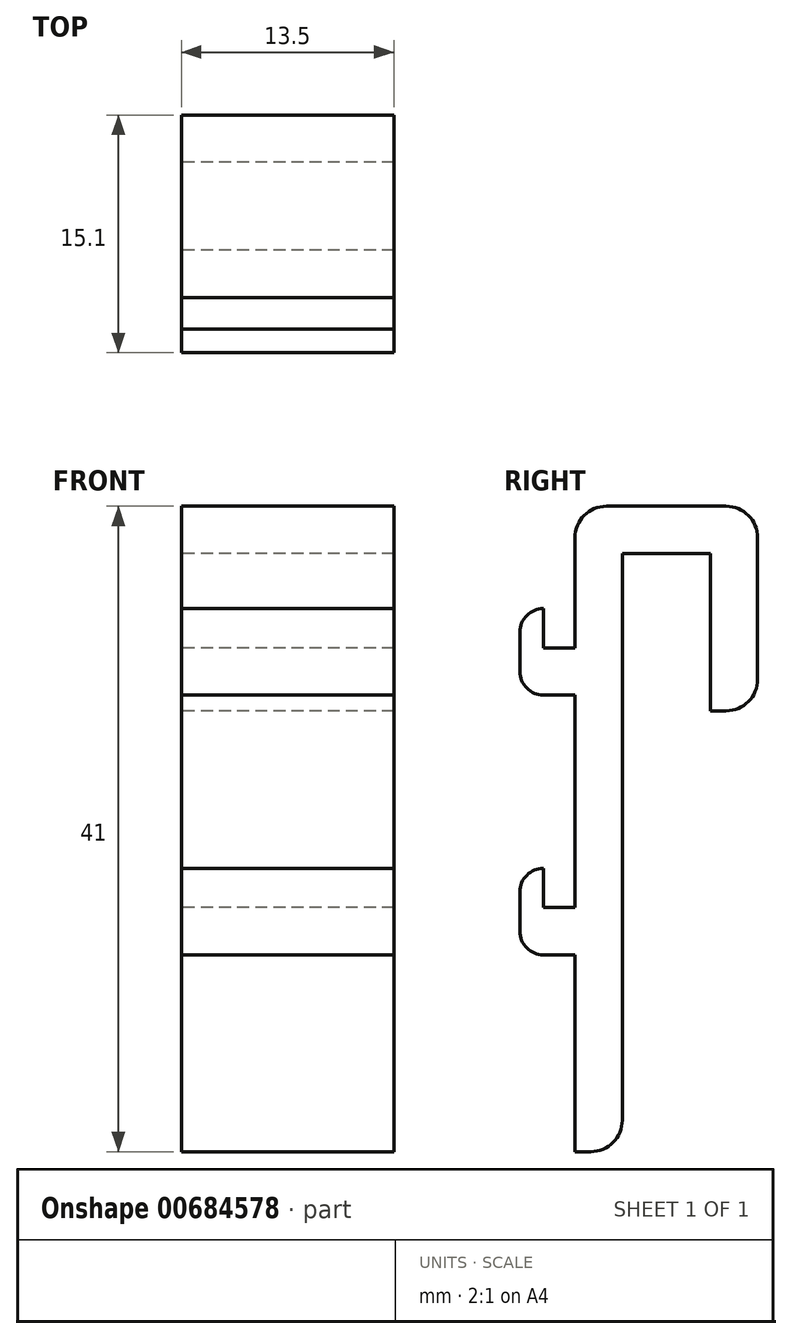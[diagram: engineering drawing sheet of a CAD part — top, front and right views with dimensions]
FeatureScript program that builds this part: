
annotation { "Feature Type Name" : "Feature", "Feature Type Description" : "" }
export const myFeature = defineFeature(function(context is Context, id is Id, definition is map)
    precondition{}
    {
        {
            var Q0;
            Q0=qCreatedBy(makeId("Top.planeOp"),FACE);
            var sketch = newSketch(context, id + "F0", { "sketchPlane" : qUnion([Q0])});
            skLineSegment(sketch, "E0", {"start": v(0, 0) * mm, "end": v(0, 12.5) * mm});
            skLineSegment(sketch, "E1", {"start": v(0, 12.5) * mm, "end": v(-3.5, 12.5) * mm});
            skLineSegment(sketch, "E2", {"start": v(-3.5, 12.5) * mm, "end": v(-3.5, 18) * mm});
            skLineSegment(sketch, "E3", {"start": v(-3.5, 18) * mm, "end": v(-2, 18) * mm});
            skLineSegment(sketch, "E4", {"start": v(-2, 18) * mm, "end": v(-2, 15.5) * mm});
            skLineSegment(sketch, "E5", {"start": v(-2, 15.5) * mm, "end": v(0, 15.5) * mm});
            skLineSegment(sketch, "E6", {"start": v(0, 15.5) * mm, "end": v(0, 29) * mm});
            skLineSegment(sketch, "E7", {"start": v(0, 29) * mm, "end": v(-3.5, 29) * mm});
            skLineSegment(sketch, "E8", {"start": v(-3.5, 29) * mm, "end": v(-3.5, 34.5) * mm});
            skLineSegment(sketch, "E9", {"start": v(-3.5, 34.5) * mm, "end": v(-2, 34.5) * mm});
            skLineSegment(sketch, "E10", {"start": v(-2, 34.5) * mm, "end": v(-2, 32) * mm});
            skLineSegment(sketch, "E11", {"start": v(-2, 32) * mm, "end": v(0, 32) * mm});
            skLineSegment(sketch, "E12", {"start": v(0, 32) * mm, "end": v(0, 41) * mm});
            skLineSegment(sketch, "E13", {"start": v(0, 41) * mm, "end": v(11.6, 41) * mm});
            skLineSegment(sketch, "E14", {"start": v(11.6, 41) * mm, "end": v(11.6, 28) * mm});
            skLineSegment(sketch, "E15", {"start": v(11.6, 28) * mm, "end": v(8.6, 28) * mm});
            skLineSegment(sketch, "E16", {"start": v(8.6, 28) * mm, "end": v(8.6, 38) * mm});
            skLineSegment(sketch, "E17", {"start": v(8.6, 38) * mm, "end": v(3, 38) * mm});
            skLineSegment(sketch, "E18", {"start": v(3, 38) * mm, "end": v(3, 0) * mm});
            skLineSegment(sketch, "E19", {"start": v(3, 0) * mm, "end": v(0, 0) * mm});
            skSolve(sketch);
        }
        {
            var Q0;
            Q0=makeQuery(id+"F0.imprint","IMPRINT",FACE,{"disambiguationData":[TD([[makeQuery(id+"F0.imprint","IMPRINT",EDGE,{"derivedFrom":sQuery(id+"F0.wireOp",EDGE,"E0")}),-1.0]])]});
            extrude(context, id + "F1", {"entities" : qUnion([Q0]), "depth" : 13.5 * mm});
        }
        {
            var Q0;
            Q0=makeQuery(id+"F1.opExtrude","SWEPT_EDGE",EDGE,{"disambiguationData":[OSD([sQuery(id+"F0.wireOp",EDGE,"E12"),sQuery(id+"F0.wireOp",EDGE,"E13")])]});
            var Q1;
            Q1=makeQuery(id+"F1.opExtrude","SWEPT_EDGE",EDGE,{"disambiguationData":[OSD([sQuery(id+"F0.wireOp",EDGE,"E13"),sQuery(id+"F0.wireOp",EDGE,"E14")])]});
            var Q2;
            Q2=makeQuery(id+"F1.opExtrude","SWEPT_EDGE",EDGE,{"disambiguationData":[OSD([sQuery(id+"F0.wireOp",EDGE,"E14"),sQuery(id+"F0.wireOp",EDGE,"E15")])]});
            var Q3;
            Q3=makeQuery(id+"F1.opExtrude","SWEPT_EDGE",EDGE,{"disambiguationData":[OSD([sQuery(id+"F0.wireOp",EDGE,"E18"),sQuery(id+"F0.wireOp",EDGE,"E19")])]});
            fillet(context, id + "F2", {"entities" : qUnion([Q0, Q1, Q2, Q3]), "radius" : 2 * mm, "tangentPropagation" : true, "allowEdgeOverflow" : false});
        }
        {
            var Q0;
            Q0=makeQuery(id+"F1.opExtrude","SWEPT_EDGE",EDGE,{"disambiguationData":[OSD([sQuery(id+"F0.wireOp",EDGE,"E8"),sQuery(id+"F0.wireOp",EDGE,"E9")])]});
            var Q1;
            Q1=makeQuery(id+"F1.opExtrude","SWEPT_EDGE",EDGE,{"disambiguationData":[OSD([sQuery(id+"F0.wireOp",EDGE,"E7"),sQuery(id+"F0.wireOp",EDGE,"E8")])]});
            var Q2;
            Q2=makeQuery(id+"F1.opExtrude","SWEPT_EDGE",EDGE,{"disambiguationData":[OSD([sQuery(id+"F0.wireOp",EDGE,"E2"),sQuery(id+"F0.wireOp",EDGE,"E3")])]});
            var Q3;
            Q3=makeQuery(id+"F1.opExtrude","SWEPT_EDGE",EDGE,{"disambiguationData":[OSD([sQuery(id+"F0.wireOp",EDGE,"E1"),sQuery(id+"F0.wireOp",EDGE,"E2")])]});
            fillet(context, id + "F3", {"entities" : qUnion([Q0, Q1, Q2, Q3]), "radius" : 1.5 * mm, "tangentPropagation" : true, "allowEdgeOverflow" : false});
        }
        {
            var Q0;
            Q0=makeQuery(id+"F1.opExtrude","SWEPT_BODY",BODY,{"disambiguationData":[OSD([sQuery(id+"F0.wireOp",EDGE,"E0"),sQuery(id+"F0.wireOp",EDGE,"E1"),sQuery(id+"F0.wireOp",EDGE,"E2"),sQuery(id+"F0.wireOp",EDGE,"E3"),sQuery(id+"F0.wireOp",EDGE,"E4"),sQuery(id+"F0.wireOp",EDGE,"E5"),sQuery(id+"F0.wireOp",EDGE,"E6"),sQuery(id+"F0.wireOp",EDGE,"E7"),sQuery(id+"F0.wireOp",EDGE,"E8"),sQuery(id+"F0.wireOp",EDGE,"E9"),sQuery(id+"F0.wireOp",EDGE,"E10"),sQuery(id+"F0.wireOp",EDGE,"E11"),sQuery(id+"F0.wireOp",EDGE,"E12"),sQuery(id+"F0.wireOp",EDGE,"E13"),sQuery(id+"F0.wireOp",EDGE,"E14"),sQuery(id+"F0.wireOp",EDGE,"E15"),sQuery(id+"F0.wireOp",EDGE,"E16"),sQuery(id+"F0.wireOp",EDGE,"E17"),sQuery(id+"F0.wireOp",EDGE,"E18"),sQuery(id+"F0.wireOp",EDGE,"E19")])]});
            var Q1;
            Q1=makeQuery(id+"F1.opExtrude","CAP_EDGE",EDGE,{"disambiguationData":[OSD([sQuery(id+"F0.wireOp",EDGE,"E0")])],"isStart":false});
            transform(context, id + "F4", {"entities" : qUnion([Q0]), "transformType" : TransformType.ROTATION, "transformAxis" : qUnion([Q1]), "angle" : 90 * degree, "makeCopy" : false});
        }
        {
            var Q0;
            Q0=makeQuery(id+"F1.opExtrude","SWEPT_BODY",BODY,{"disambiguationData":[OSD([sQuery(id+"F0.wireOp",EDGE,"E0"),sQuery(id+"F0.wireOp",EDGE,"E1"),sQuery(id+"F0.wireOp",EDGE,"E2"),sQuery(id+"F0.wireOp",EDGE,"E3"),sQuery(id+"F0.wireOp",EDGE,"E4"),sQuery(id+"F0.wireOp",EDGE,"E5"),sQuery(id+"F0.wireOp",EDGE,"E6"),sQuery(id+"F0.wireOp",EDGE,"E7"),sQuery(id+"F0.wireOp",EDGE,"E8"),sQuery(id+"F0.wireOp",EDGE,"E9"),sQuery(id+"F0.wireOp",EDGE,"E10"),sQuery(id+"F0.wireOp",EDGE,"E11"),sQuery(id+"F0.wireOp",EDGE,"E12"),sQuery(id+"F0.wireOp",EDGE,"E13"),sQuery(id+"F0.wireOp",EDGE,"E14"),sQuery(id+"F0.wireOp",EDGE,"E15"),sQuery(id+"F0.wireOp",EDGE,"E16"),sQuery(id+"F0.wireOp",EDGE,"E17"),sQuery(id+"F0.wireOp",EDGE,"E18"),sQuery(id+"F0.wireOp",EDGE,"E19")])]});
            var Q1;
            Q1=makeQuery(id+"F1.opExtrude","SWEPT_EDGE",EDGE,{"disambiguationData":[OSD([sQuery(id+"F0.wireOp",EDGE,"E0"),sQuery(id+"F0.wireOp",EDGE,"E19")])]});
            transform(context, id + "F5", {"entities" : qUnion([Q0]), "transformType" : TransformType.ROTATION, "transformAxis" : qUnion([Q1]), "angle" : 270 * degree, "makeCopy" : false});
        }
    });
